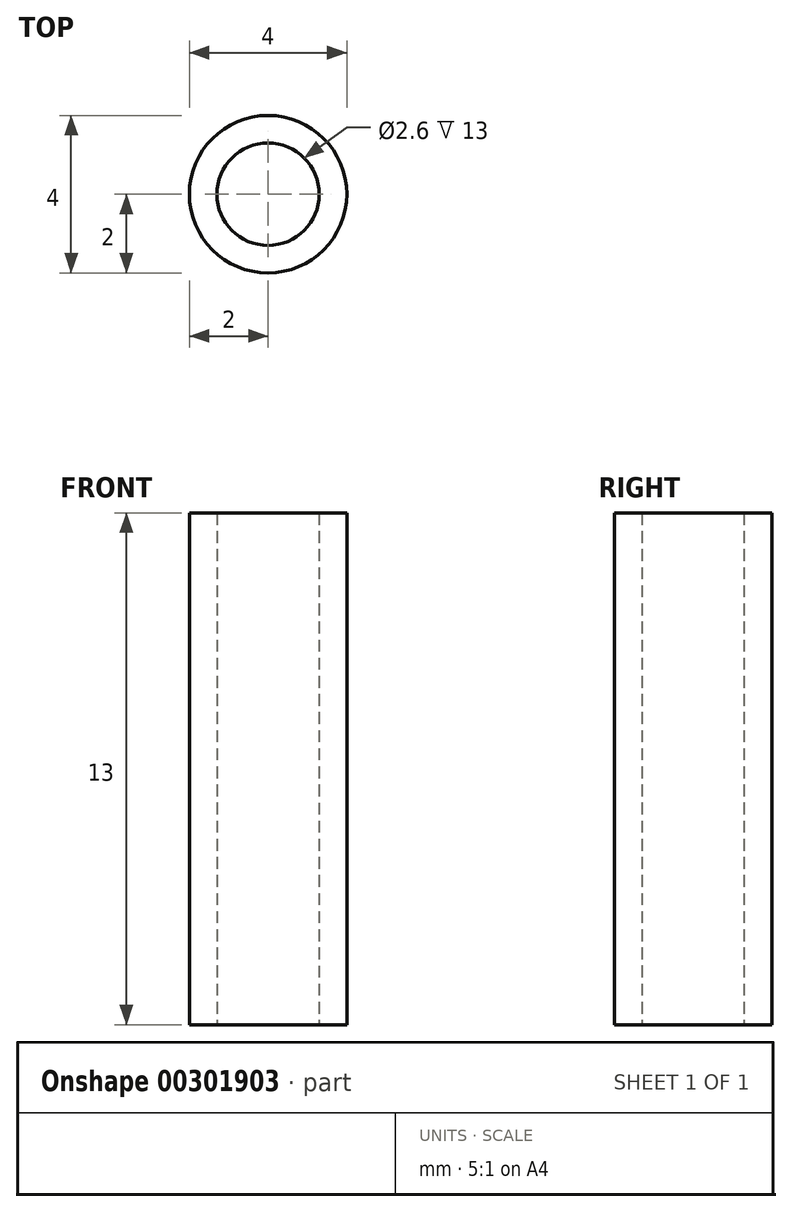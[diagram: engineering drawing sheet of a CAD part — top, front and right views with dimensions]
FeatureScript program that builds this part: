
annotation { "Feature Type Name" : "Feature", "Feature Type Description" : "" }
export const myFeature = defineFeature(function(context is Context, id is Id, definition is map)
    precondition{}
    {
        {
            var Q0;
            Q0=qCreatedBy(makeId("Top.planeOp"),FACE);
            var sketch = newSketch(context, id + "F0", { "sketchPlane" : qUnion([Q0])});
            skCircle(sketch, "E0", {"center": v(0, 0) * mm, "radius": 1.3 * mm});
            skCircle(sketch, "E1", {"center": v(0, 0) * mm, "radius": 2 * mm});
            skSolve(sketch);
        }
        {
            var Q0;
            Q0=makeQuery(id+"F0.imprint","IMPRINT",FACE,{"disambiguationData":[TD([[makeQuery(id+"F0.imprint","IMPRINT",EDGE,{"derivedFrom":sQuery(id+"F0.wireOp",EDGE,"E0")}),-1.0]])]});
            extrude(context, id + "F1", {"entities" : qUnion([Q0]), "depth" : 13 * mm});
        }
    });
